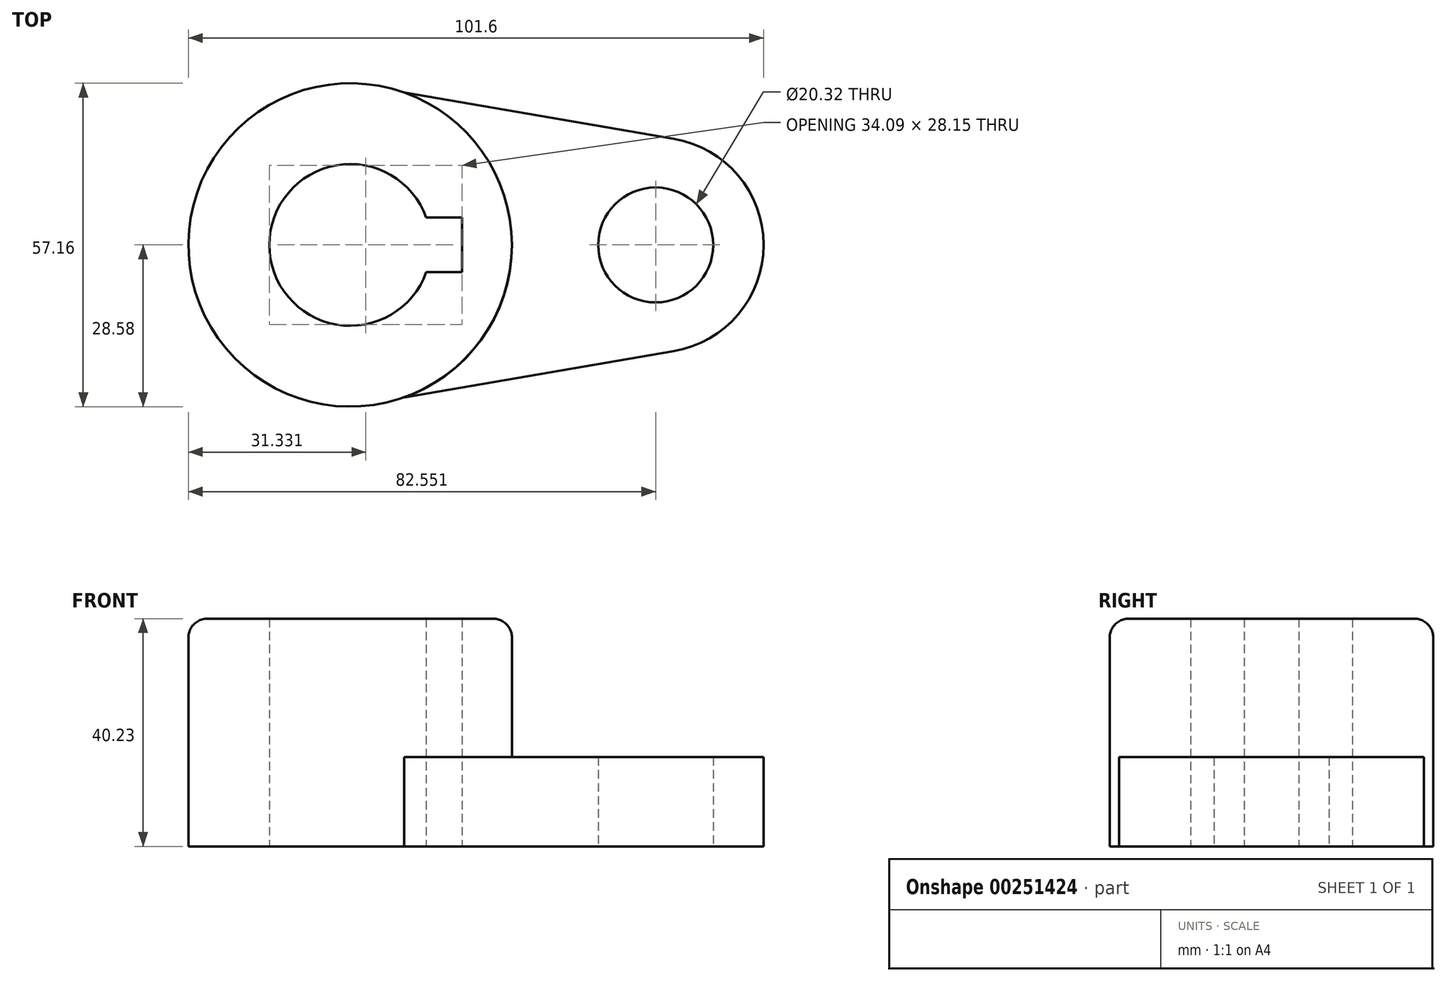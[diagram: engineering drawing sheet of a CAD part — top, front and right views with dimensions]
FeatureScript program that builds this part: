
annotation { "Feature Type Name" : "Feature", "Feature Type Description" : "" }
export const myFeature = defineFeature(function(context is Context, id is Id, definition is map)
    precondition{}
    {
        {
            var Q0;
            Q0=qCreatedBy(makeId("Top.planeOp"),FACE);
            var sketch = newSketch(context, id + "F0", { "sketchPlane" : qUnion([Q0])});
            skArc(sketch, "E0", {"start": v(-15.22, 4.83) * mm, "mid": v(-42.95, 0) * mm, "end": v(-15.22, -4.83) * mm});
            skCircle(sketch, "E1", {"center": v(25.31, 0) * mm, "radius": 10.16 * mm});
            skCircle(sketch, "E2", {"center": v(-28.66, 0) * mm, "radius": 28.58 * mm});
            skCircle(sketch, "E3", {"center": v(25.31, 0) * mm, "radius": 19.05 * mm});
            skPoint(sketch, "E4.visualSharp", {"position": v(33.04, -28.58) * mm});
            skLineSegment(sketch, "E5", {"start": v(-19.15, -26.95) * mm, "end": v(28.53, -18.78) * mm});
            skLineSegment(sketch, "E6", {"start": v(-19.15, 26.95) * mm, "end": v(28.53, 18.78) * mm});
            skLineSegment(sketch, "E7.right", {"start": v(-8.87, -4.83) * mm, "end": v(-8.87, 4.83) * mm});
            skLineSegment(sketch, "E8.trimOffspring", {"start": v(-15.22, 4.83) * mm, "end": v(-8.87, 4.83) * mm});
            skLineSegment(sketch, "E9.trimOffspring", {"start": v(-15.22, -4.83) * mm, "end": v(-8.87, -4.83) * mm});
            skLineSegment(sketch, "E10", {"start": v(-28.66, 0) * mm, "end": v(25.31, 0) * mm, "construction": true});
            skPoint(sketch, "E11.orphan", {"position": v(-28.66, 28.58) * mm});
            skPoint(sketch, "E12.orphan", {"position": v(-28.66, -28.57) * mm});
            skSolve(sketch);
        }
        {
            var Q0;
            Q0=makeQuery(id+"F0.imprint","IMPRINT",FACE,{"disambiguationData":[TD([[makeQuery(id+"F0.imprint","IMPRINT",EDGE,{"derivedFrom":sQuery(id+"F0.wireOp",EDGE,"E0")}),-1.0]])]});
            extrude(context, id + "F1", {"entities" : qUnion([Q0]), "depth" : 40.23 * mm});
        }
        {
            var Q0;
            {var subQ0=sQuery(id+"F0.wireOp",EDGE,"E6");var subQ1=sQuery(id+"F0.wireOp",EDGE,"E2");var subQ2=makeQuery(id+"F0.imprint","INTERSECT",VERTEX,{"disambiguationData":[OD(1.0)],"derivedFrom":[subQ1,subQ0]});Q0=makeQuery(id+"F0.imprint","IMPRINT",FACE,{"disambiguationData":[TD([[makeQuery(id+"F0.imprint","IMPRINT",EDGE,{"disambiguationData":[TD([[subQ2,1.0]])],"derivedFrom":subQ1}),-1.0]])]});}
            var Q1;
            Q1=makeQuery(id+"F0.imprint","IMPRINT",FACE,{"disambiguationData":[TD([[makeQuery(id+"F0.imprint","IMPRINT",EDGE,{"derivedFrom":sQuery(id+"F0.wireOp",EDGE,"E1")}),-1.0]])]});
            extrude(context, id + "F2", {"entities" : qUnion([Q0, Q1]), "operationType" : NewBodyOperationType.ADD, "depth" : 15.77 * mm});
        }
        {
            var Q0;
            {var subQ0=sQuery(id+"F0.wireOp",EDGE,"E2");Q0=makeQuery(id+"F1.opExtrude","CAP_EDGE",EDGE,{"disambiguationData":[OSD([subQ0]),TDD([makeQuery(id+"F0.imprint","IMPRINT",EDGE,{"disambiguationData":[TD([[makeQuery(id+"F0.imprint","INTERSECT",VERTEX,{"disambiguationData":[OD(0.0)],"derivedFrom":[subQ0,sQuery(id+"F0.wireOp",EDGE,"E5")]}),1.0]])],"derivedFrom":subQ0})])],"isStart":false});}
            var Q1;
            Q1=makeQuery(id+"F1.opExtrude","CAP_EDGE",EDGE,{"disambiguationData":[OSD([sQuery(id+"F0.wireOp",EDGE,"E5")])],"isStart":false});
            var Q2;
            {var subQ0=sQuery(id+"F0.wireOp",EDGE,"E2");Q2=makeQuery(id+"F1.opExtrude","CAP_EDGE",EDGE,{"disambiguationData":[OSD([subQ0]),TDD([makeQuery(id+"F0.imprint","IMPRINT",EDGE,{"disambiguationData":[TD([[makeQuery(id+"F0.imprint","INTERSECT",VERTEX,{"disambiguationData":[OD(1.0)],"derivedFrom":[subQ0,sQuery(id+"F0.wireOp",EDGE,"E6")]}),1.0]])],"derivedFrom":subQ0})])],"isStart":false});}
            var Q3;
            Q3=makeQuery(id+"F1.opExtrude","CAP_EDGE",EDGE,{"disambiguationData":[OSD([sQuery(id+"F0.wireOp",EDGE,"E6")])],"isStart":false});
            fillet(context, id + "F3", {"entities" : qUnion([Q0, Q1, Q2, Q3]), "radius" : 3.3 * mm, "tangentPropagation" : true, "allowEdgeOverflow" : false});
        }
    });
